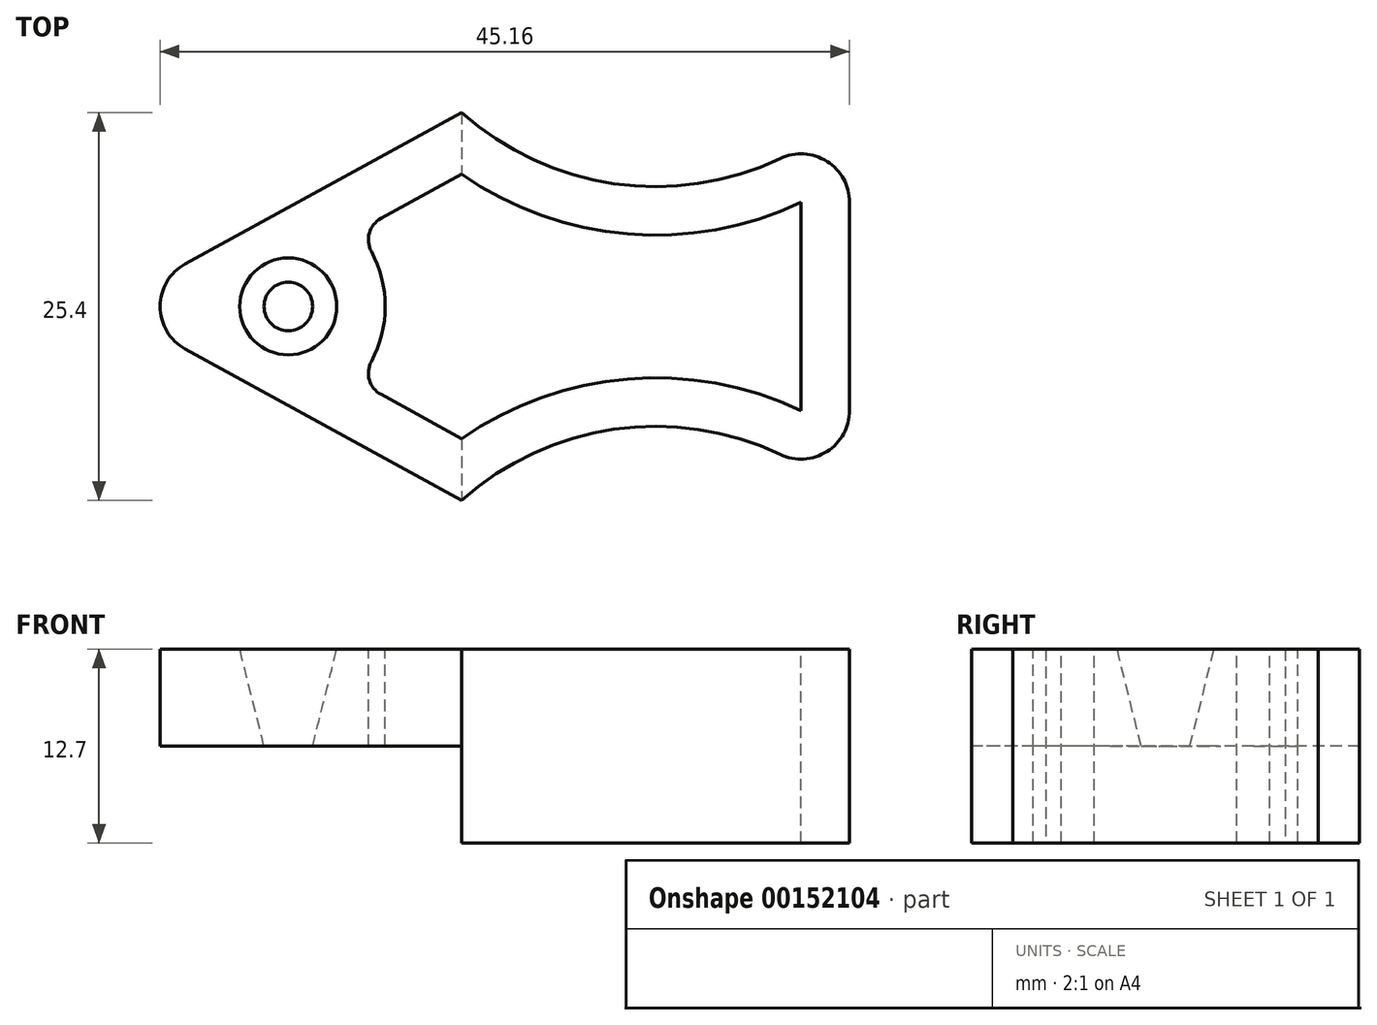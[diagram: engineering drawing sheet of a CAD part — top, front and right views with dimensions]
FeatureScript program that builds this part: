
annotation { "Feature Type Name" : "Feature", "Feature Type Description" : "" }
export const myFeature = defineFeature(function(context is Context, id is Id, definition is map)
    precondition{}
    {
        {
            var Q0;
            Q0=qCreatedBy(makeId("Top.planeOp"),FACE);
            var sketch = newSketch(context, id + "F0", { "sketchPlane" : qUnion([Q0])});
            skLineSegment(sketch, "E0.bottom", {"start": v(-25.4, 0) * mm, "end": v(-34.56, 0) * mm});
            skLineSegment(sketch, "E0.top", {"start": v(-25.4, 25.4) * mm, "end": v(-34.56, 25.4) * mm});
            skLineSegment(sketch, "E0.left", {"start": v(0, 5.88) * mm, "end": v(0, 19.52) * mm});
            skLineSegment(sketch, "E0.right", {"start": v(-34.56, 0) * mm, "end": v(-34.56, 25.4) * mm});
            skArc(sketch, "E1", {"start": v(-4.54, 3.01) * mm, "mid": v(-15.42, 4.66) * mm, "end": v(-25.4, 0) * mm});
            skArc(sketch, "E2", {"start": v(-25.4, 25.4) * mm, "mid": v(-15.42, 20.74) * mm, "end": v(-4.54, 22.39) * mm});
            skPoint(sketch, "E3.visualSharp", {"position": v(0, 25.4) * mm});
            skArc(sketch, "E3.filletArc", {"start": v(0, 19.52) * mm, "mid": v(-1.48, 22.2) * mm, "end": v(-4.54, 22.39) * mm});
            skPoint(sketch, "E4.visualSharp", {"position": v(0, 0) * mm});
            skArc(sketch, "E4.filletArc", {"start": v(-4.54, 3.01) * mm, "mid": v(-1.48, 3.2) * mm, "end": v(0, 5.88) * mm});
            skCircle(sketch, "E5", {"center": v(-36.76, 12.7) * mm, "radius": 17.04 * mm});
            skPoint(sketch, "E6", {"position": v(-34.56, 12.7) * mm});
            skSolve(sketch);
        }
        {
            var Q0;
            {var subQ0=sQuery(id+"F0.wireOp",EDGE,"E0.bottom");Q0=makeQuery(id+"F0.imprint","IMPRINT",FACE,{"disambiguationData":[TD([[makeQuery(id+"F0.imprint","IMPRINT",EDGE,{"derivedFrom":subQ0}),1.0]])]});}
            var Q1;
            {var subQ0=sQuery(id+"F0.wireOp",EDGE,"E0.bottom");Q1=makeQuery(id+"F0.imprint","IMPRINT",FACE,{"disambiguationData":[TD([[makeQuery(id+"F0.imprint","IMPRINT",EDGE,{"derivedFrom":subQ0}),-1.0]])]});}
            var Q2;
            Q2=makeQuery(id+"F0.imprint","IMPRINT",FACE,{"disambiguationData":[TD([[makeQuery(id+"F0.imprint","IMPRINT",EDGE,{"derivedFrom":sQuery(id+"F0.wireOp",EDGE,"E0.left")}),1.0]])]});
            extrude(context, id + "F1", {"entities" : qUnion([Q0, Q1, Q2]), "depth" : 12.7 * mm});
        }
        {
            var Q0;
            Q0=makeQuery(id+"F1.opExtrude","CAP_FACE",FACE,{"disambiguationData":[OSD([sQuery(id+"F0.wireOp",EDGE,"E0.left"),sQuery(id+"F0.wireOp",EDGE,"E1"),sQuery(id+"F0.wireOp",EDGE,"E2"),sQuery(id+"F0.wireOp",EDGE,"E3.filletArc"),sQuery(id+"F0.wireOp",EDGE,"E4.filletArc"),sQuery(id+"F0.wireOp",EDGE,"E5")])],"isStart":false});
            var sketch = newSketch(context, id + "F2", { "sketchPlane" : qUnion([Q0])});
            skCircle(sketch, "E7", {"center": v(-36.76, 12.7) * mm, "radius": 3.18 * mm});
            skSolve(sketch);
        }
        {
            var Q0;
            Q0 = qSketchRegion(id + "F2", true);
            var Q1;
            Q1=makeQuery(id+"F1.opExtrude","CAP_FACE",FACE,{"disambiguationData":[OSD([sQuery(id+"F0.wireOp",EDGE,"E0.left"),sQuery(id+"F0.wireOp",EDGE,"E1"),sQuery(id+"F0.wireOp",EDGE,"E2"),sQuery(id+"F0.wireOp",EDGE,"E3.filletArc"),sQuery(id+"F0.wireOp",EDGE,"E4.filletArc"),sQuery(id+"F0.wireOp",EDGE,"E5")])],"isStart":true});
            extrude(context, id + "F3", {"entities" : qUnion([Q0]), "operationType" : NewBodyOperationType.REMOVE, "endBound" : BoundingType.UP_TO_NEXT, "oppositeDirection" : true, "endBoundEntityFace" : qUnion([Q1]), "depth" : 25.4 * mm, "hasDraft" : true, "draftAngle" : 14 * degree, "draftPullDirection" : true});
        }
        {
            var Q0;
            Q0=makeQuery(id+"F1.opExtrude","CAP_FACE",FACE,{"disambiguationData":[OSD([sQuery(id+"F0.wireOp",EDGE,"E0.left"),sQuery(id+"F0.wireOp",EDGE,"E1"),sQuery(id+"F0.wireOp",EDGE,"E2"),sQuery(id+"F0.wireOp",EDGE,"E3.filletArc"),sQuery(id+"F0.wireOp",EDGE,"E4.filletArc"),sQuery(id+"F0.wireOp",EDGE,"E5")])],"isStart":false});
            var sketch = newSketch(context, id + "F4", { "sketchPlane" : qUnion([Q0])});
            skLineSegment(sketch, "E8", {"start": v(-25.4, 0) * mm, "end": v(-43.5, 9.92) * mm});
            skLineSegment(sketch, "E9", {"start": v(-43.5, 15.48) * mm, "end": v(-25.4, 25.4) * mm});
            skPoint(sketch, "E10", {"position": v(0, 12.7) * mm});
            skPoint(sketch, "E11.visualSharp", {"position": v(-48.6, 12.7) * mm});
            skArc(sketch, "E11.filletArc", {"start": v(-43.5, 15.48) * mm, "mid": v(-45.16, 12.7) * mm, "end": v(-43.5, 9.92) * mm});
            skArc(sketch, "E12.0", {"start": v(-3.18, 5.88) * mm, "mid": v(-14.54, 7.95) * mm, "end": v(-25.4, 4.04) * mm});
            skLineSegment(sketch, "E12.1", {"start": v(-3.18, 5.88) * mm, "end": v(-3.18, 19.52) * mm});
            skArc(sketch, "E12.2", {"start": v(-25.4, 21.36) * mm, "mid": v(-14.54, 17.45) * mm, "end": v(-3.17, 19.52) * mm});
            skLineSegment(sketch, "E13", {"start": v(-25.4, 4.04) * mm, "end": v(-30.7, 6.94) * mm});
            skLineSegment(sketch, "E14", {"start": v(-25.4, 21.36) * mm, "end": v(-30.7, 18.46) * mm});
            skArc(sketch, "E15", {"start": v(-31.32, 9.09) * mm, "mid": v(-30.4, 12.7) * mm, "end": v(-31.32, 16.31) * mm});
            skPoint(sketch, "E16", {"position": v(-33.58, 12.7) * mm});
            skPoint(sketch, "E17", {"position": v(-30.4, 12.7) * mm});
            skPoint(sketch, "E18.visualSharp", {"position": v(-32.22, 7.78) * mm});
            skArc(sketch, "E18.filletArc", {"start": v(-31.32, 9.09) * mm, "mid": v(-31.45, 7.88) * mm, "end": v(-30.7, 6.94) * mm});
            skPoint(sketch, "E19.visualSharp", {"position": v(-32.22, 17.62) * mm});
            skArc(sketch, "E19.filletArc", {"start": v(-30.7, 18.46) * mm, "mid": v(-31.45, 17.52) * mm, "end": v(-31.32, 16.31) * mm});
            skSolve(sketch);
        }
        {
            var Q0;
            Q0=makeQuery(id+"F4.imprint","IMPRINT",FACE,{"disambiguationData":[TD([[makeQuery(id+"F4.imprint","IMPRINT",EDGE,{"derivedFrom":sQuery(id+"F4.wireOp",EDGE,"E12.0")}),-1.0]])]});
            var Q1;
            Q1=makeQuery(id+"F4.imprint","IMPRINT",FACE,{"disambiguationData":[TD([[makeQuery(id+"F4.imprint","IMPRINT",EDGE,{"derivedFrom":sQuery(id+"F4.wireOp",EDGE,"E8")}),1.0]])]});
            extrude(context, id + "F5", {"entities" : qUnion([Q0, Q1]), "operationType" : NewBodyOperationType.REMOVE, "endBound" : BoundingType.THROUGH_ALL, "oppositeDirection" : true, "depth" : 25.4 * mm});
        }
        {
            var Q0;
            Q0=qCreatedBy(makeId("Front.planeOp"),FACE);
            var sketch = newSketch(context, id + "F6", { "sketchPlane" : qUnion([Q0])});
            skLineSegment(sketch, "E20.bottom", {"start": v(-25.4, 0) * mm, "end": v(-63.5, 0) * mm});
            skLineSegment(sketch, "E20.top", {"start": v(-25.4, 6.35) * mm, "end": v(-63.5, 6.35) * mm});
            skLineSegment(sketch, "E20.left", {"start": v(-25.4, 0) * mm, "end": v(-25.4, 6.35) * mm});
            skLineSegment(sketch, "E20.right", {"start": v(-63.5, 0) * mm, "end": v(-63.5, 6.35) * mm});
            skSolve(sketch);
        }
        {
            var Q0;
            Q0=makeQuery(id+"F6.imprint","IMPRINT",FACE,{"disambiguationData":[TD([[makeQuery(id+"F6.imprint","IMPRINT",EDGE,{"derivedFrom":sQuery(id+"F6.wireOp",EDGE,"E20.bottom")}),-1.0]])]});
            extrude(context, id + "F7", {"entities" : qUnion([Q0]), "operationType" : NewBodyOperationType.REMOVE, "endBound" : BoundingType.THROUGH_ALL, "oppositeDirection" : true, "depth" : 25.4 * mm});
        }
    });
